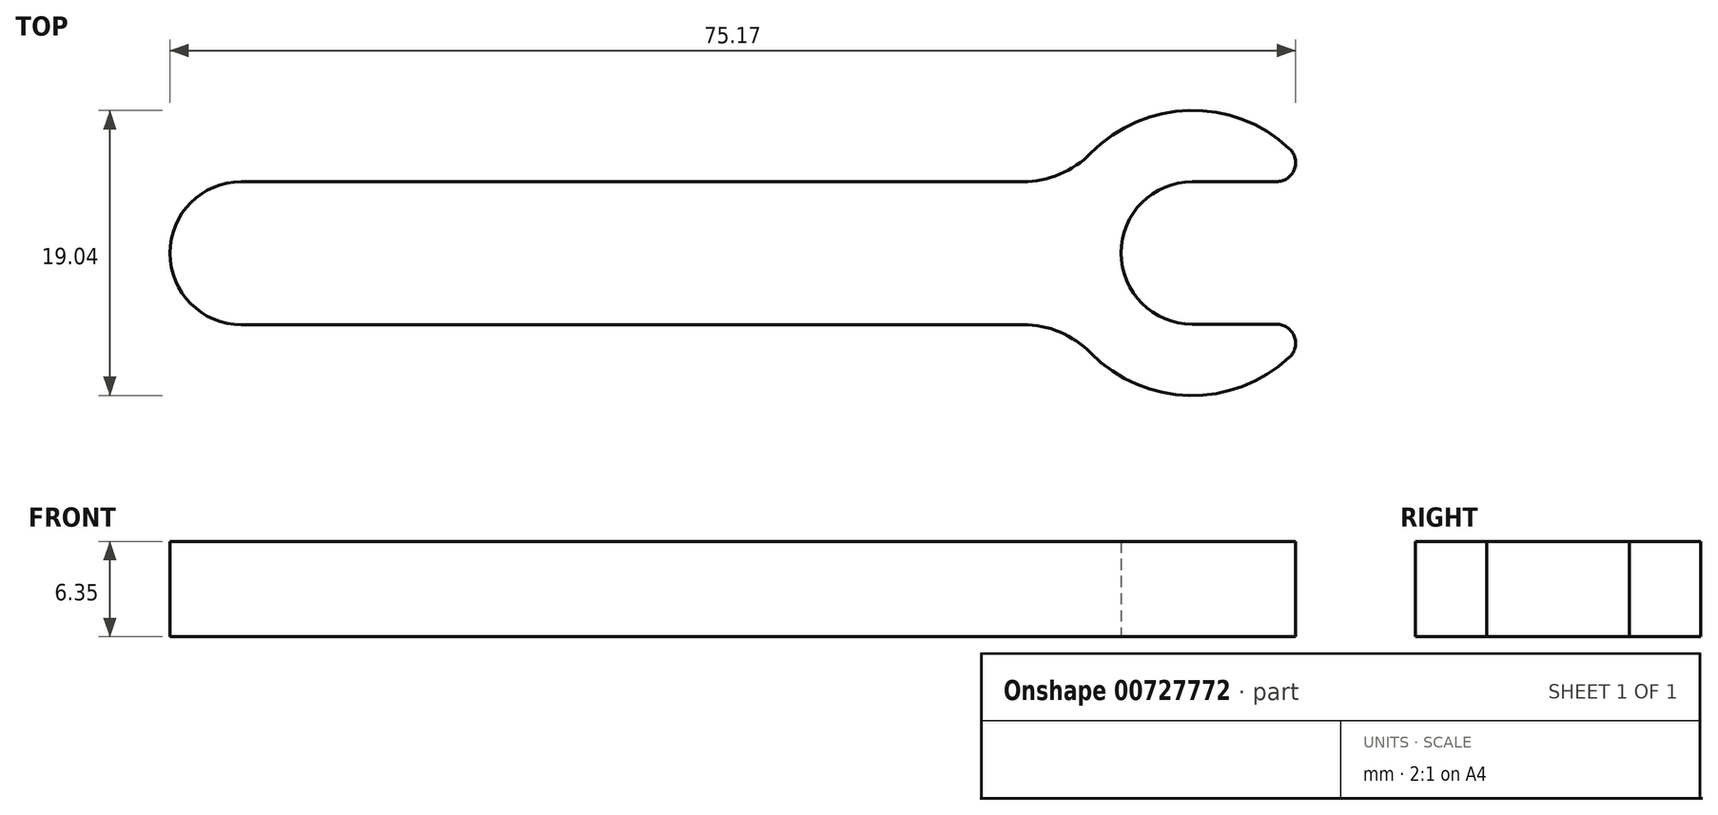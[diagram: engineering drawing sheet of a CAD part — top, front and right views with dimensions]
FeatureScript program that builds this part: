
annotation { "Feature Type Name" : "Feature", "Feature Type Description" : "" }
export const myFeature = defineFeature(function(context is Context, id is Id, definition is map)
    precondition{}
    {
        {
            var Q0;
            Q0=qCreatedBy(makeId("Top.planeOp"),FACE);
            var sketch = newSketch(context, id + "F0", { "sketchPlane" : qUnion([Q0])});
            skLineSegment(sketch, "E0", {"start": v(0, -4.78) * mm, "end": v(52.19, -4.78) * mm});
            skLineSegment(sketch, "E1", {"start": v(0, 4.78) * mm, "end": v(52.18, 4.78) * mm});
            skArc(sketch, "E2", {"start": v(0, 4.78) * mm, "mid": v(-4.78, 0) * mm, "end": v(0, -4.78) * mm});
            skArc(sketch, "E3", {"start": v(69.99, 6.97) * mm, "mid": v(63.29, 9.53) * mm, "end": v(56.7, 6.68) * mm});
            skArc(sketch, "E4", {"start": v(56.7, -6.67) * mm, "mid": v(63.3, -9.5) * mm, "end": v(69.99, -6.95) * mm});
            skLineSegment(sketch, "E5", {"start": v(69.12, -4.75) * mm, "end": v(63.5, -4.75) * mm});
            skLineSegment(sketch, "E6", {"start": v(69.12, 4.78) * mm, "end": v(63.5, 4.78) * mm});
            skArc(sketch, "E7", {"start": v(63.5, 4.78) * mm, "mid": v(58.74, 0.01) * mm, "end": v(63.5, -4.75) * mm});
            skPoint(sketch, "E8.visualSharp", {"position": v(71.74, 4.78) * mm});
            skArc(sketch, "E8.filletArc", {"start": v(69.12, 4.78) * mm, "mid": v(70.3, 5.58) * mm, "end": v(69.99, 6.97) * mm});
            skPoint(sketch, "E9.visualSharp", {"position": v(71.74, -4.75) * mm});
            skArc(sketch, "E9.filletArc", {"start": v(69.99, -6.95) * mm, "mid": v(70.3, -5.55) * mm, "end": v(69.12, -4.75) * mm});
            skPoint(sketch, "E10.visualSharp", {"position": v(55.26, -4.78) * mm});
            skArc(sketch, "E10.filletArc", {"start": v(56.7, -6.67) * mm, "mid": v(54.64, -5.27) * mm, "end": v(52.19, -4.78) * mm});
            skPoint(sketch, "E11.visualSharp", {"position": v(55.26, 4.78) * mm});
            skArc(sketch, "E11.filletArc", {"start": v(52.18, 4.78) * mm, "mid": v(54.63, 5.27) * mm, "end": v(56.7, 6.68) * mm});
            skLineSegment(sketch, "E12", {"start": v(0, 0) * mm, "end": v(69.12, 0.01) * mm, "construction": true});
            skSolve(sketch);
        }
        {
            var Q0;
            Q0 = qSketchRegion(id + "F0", true);
            extrude(context, id + "F1", {"entities" : qUnion([Q0]), "depth" : 6.35 * mm, "offsetDistance" : 25.4 * mm});
        }
    });
